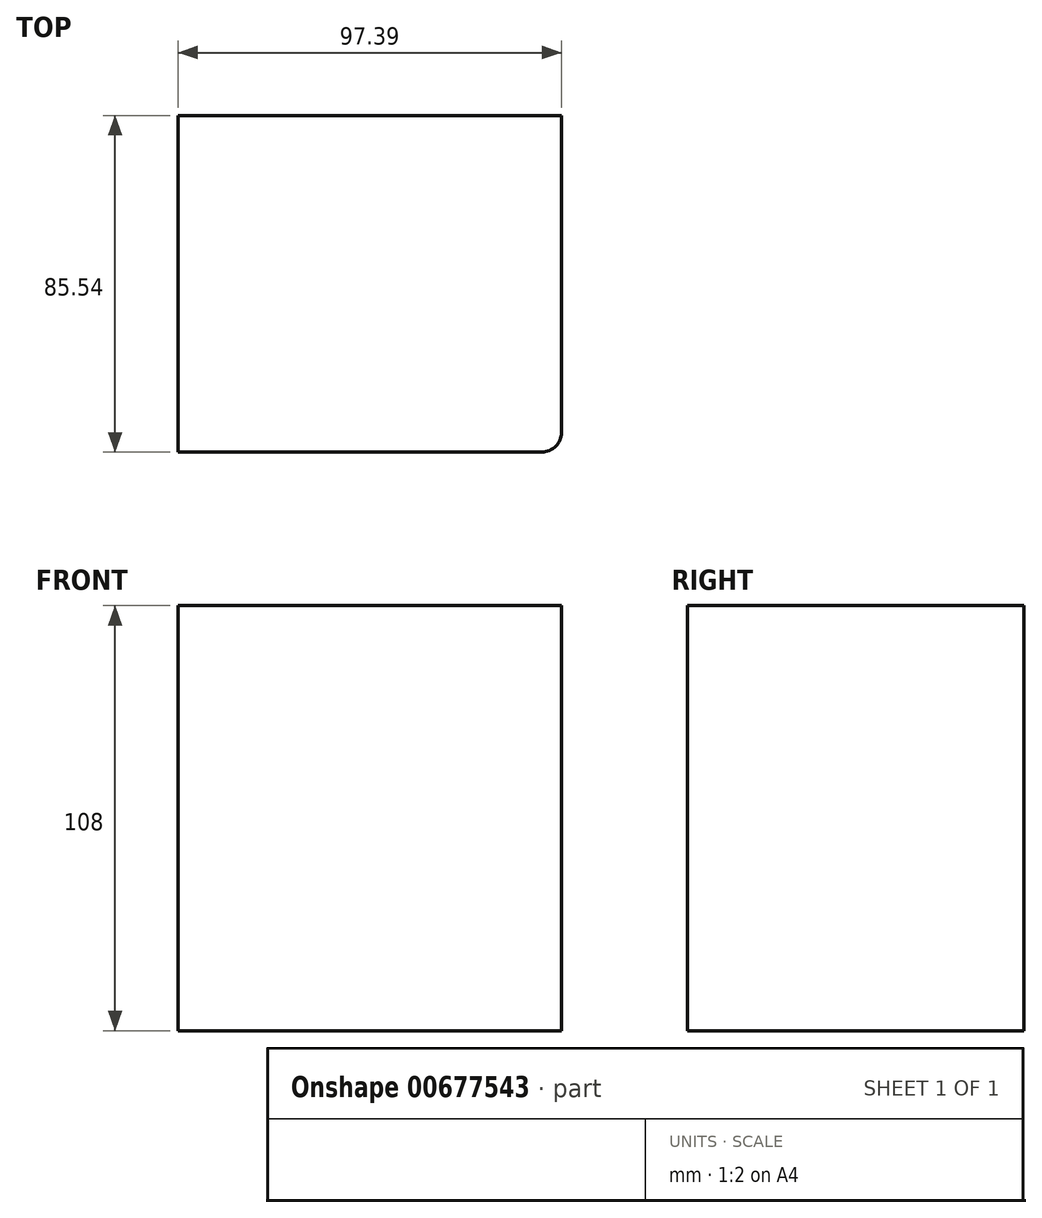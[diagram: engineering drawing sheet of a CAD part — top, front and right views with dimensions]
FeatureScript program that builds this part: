
annotation { "Feature Type Name" : "Feature", "Feature Type Description" : "" }
export const myFeature = defineFeature(function(context is Context, id is Id, definition is map)
    precondition{}
    {
        {
            var Q0;
            Q0=qCreatedBy(makeId("Top.planeOp"),FACE);
            var sketch = newSketch(context, id + "F0", { "sketchPlane" : qUnion([Q0])});
            skLineSegment(sketch, "E0.bottom", {"start": v(-44.94, -41.98) * mm, "end": v(52.45, -41.98) * mm});
            skLineSegment(sketch, "E0.top", {"start": v(-44.94, 43.56) * mm, "end": v(52.45, 43.56) * mm});
            skLineSegment(sketch, "E0.left", {"start": v(-44.94, -41.98) * mm, "end": v(-44.94, 43.56) * mm});
            skLineSegment(sketch, "E0.right", {"start": v(52.45, -41.98) * mm, "end": v(52.45, 43.56) * mm});
            skSolve(sketch);
        }
        {
            var Q0;
            Q0=makeQuery(id+"F0.imprint","IMPRINT",FACE,{"disambiguationData":[TD([[makeQuery(id+"F0.imprint","IMPRINT",EDGE,{"derivedFrom":sQuery(id+"F0.wireOp",EDGE,"E0.bottom")}),1.0]])]});
            extrude(context, id + "F1", {"entities" : qUnion([Q0]), "depth" : 108 * mm, "offsetDistance" : 25 * mm});
        }
        {
            var Q0;
            Q0=makeQuery(id+"F1.opExtrude","SWEPT_EDGE",EDGE,{"disambiguationData":[OSD([sQuery(id+"F0.wireOp",EDGE,"E0.bottom"),sQuery(id+"F0.wireOp",EDGE,"E0.right")])]});
            fillet(context, id + "F2", {"entities" : qUnion([Q0]), "radius" : 5 * mm, "tangentPropagation" : true, "allowEdgeOverflow" : false});
        }
        {
            var Q0;
            Q0=makeQuery(id+"F1.opExtrude","SWEPT_FACE",FACE,{"disambiguationData":[OSD([sQuery(id+"F0.wireOp",EDGE,"E0.bottom")])]});
            var sketch = newSketch(context, id + "F3", { "sketchPlane" : qUnion([Q0])});
            skLineSegment(sketch, "E1", {"start": v(-44.94, 108) * mm, "end": v(47.45, 0) * mm});
            skLineSegment(sketch, "E2", {"start": v(47.45, 108) * mm, "end": v(-44.94, 0) * mm});
            skSolve(sketch);
        }
    });
